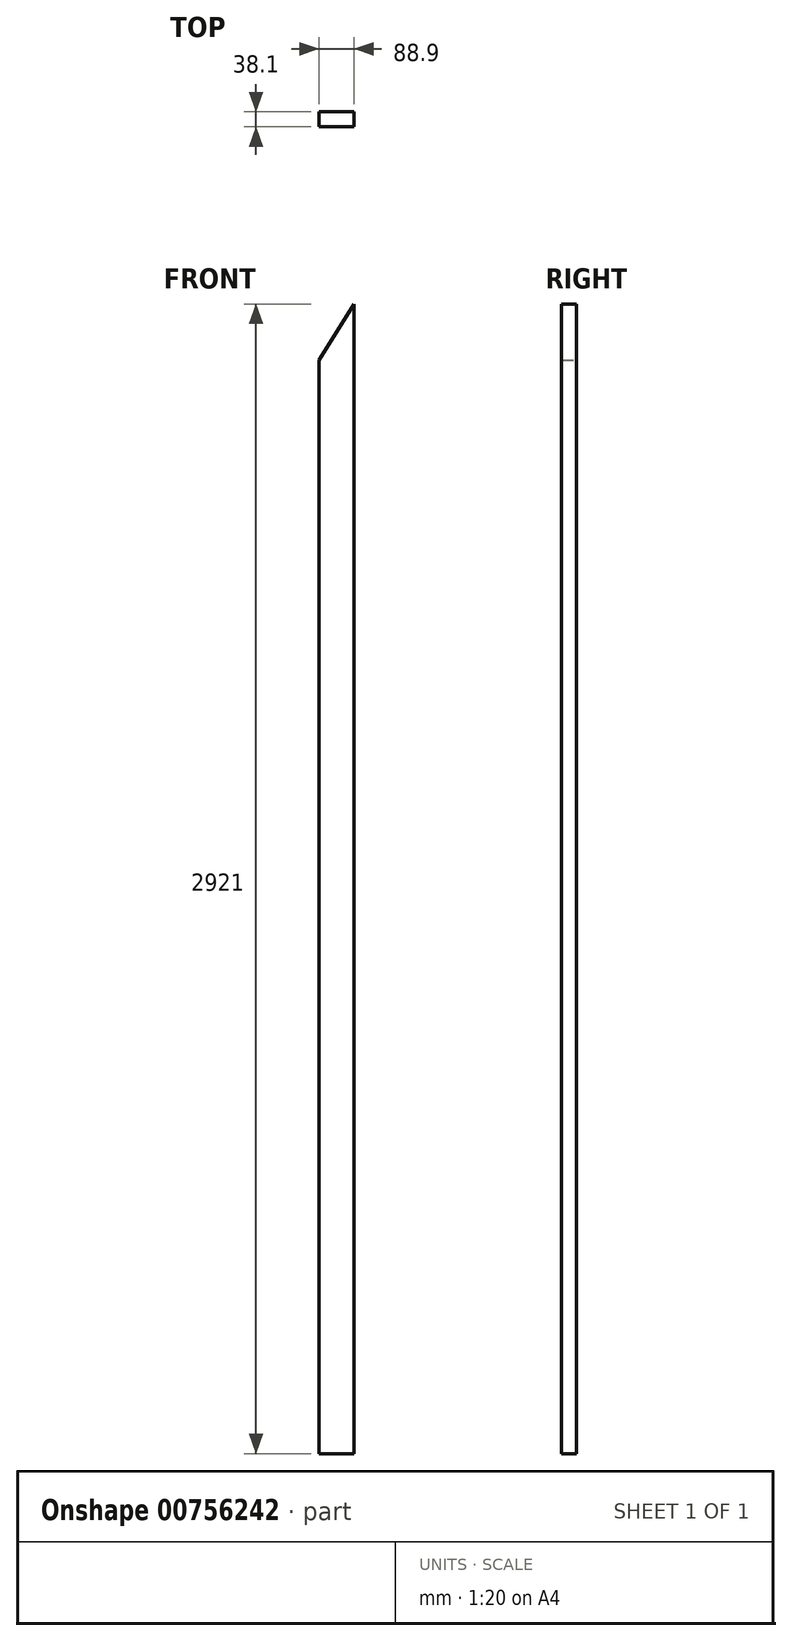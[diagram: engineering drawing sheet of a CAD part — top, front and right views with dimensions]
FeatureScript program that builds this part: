
annotation { "Feature Type Name" : "Feature", "Feature Type Description" : "" }
export const myFeature = defineFeature(function(context is Context, id is Id, definition is map)
    precondition{}
    {
        {
            var Q0;
            Q0=qCreatedBy(makeId("Front.planeOp"),FACE);
            var sketch = newSketch(context, id + "F0", { "sketchPlane" : qUnion([Q0])});
            skLineSegment(sketch, "E0.bottom", {"start": v(-44.45, 1460.5) * mm, "end": v(44.45, 1460.5) * mm});
            skLineSegment(sketch, "E0.top", {"start": v(-44.45, -1460.5) * mm, "end": v(44.45, -1460.5) * mm});
            skLineSegment(sketch, "E0.left", {"start": v(-44.45, 1460.5) * mm, "end": v(-44.45, -1460.5) * mm});
            skLineSegment(sketch, "E0.right", {"start": v(44.45, 1460.5) * mm, "end": v(44.45, -1460.5) * mm});
            skPoint(sketch, "E0.middle", {"position": v(0, 0) * mm});
            skLineSegment(sketch, "E1", {"start": v(44.45, 1460.5) * mm, "end": v(-44.45, 1318.23) * mm});
            skSolve(sketch);
        }
        {
            var Q0;
            {var subQ0=sQuery(id+"F0.wireOp",EDGE,"E0.top");Q0=makeQuery(id+"F0.imprint","IMPRINT",FACE,{"disambiguationData":[TD([[makeQuery(id+"F0.imprint","IMPRINT",EDGE,{"derivedFrom":subQ0}),1.0]])]});}
            extrude(context, id + "F1", {"entities" : qUnion([Q0]), "endBound" : BoundingType.SYMMETRIC, "depth" : 38.1 * mm, "offsetDistance" : 25.4 * mm});
        }
    });
